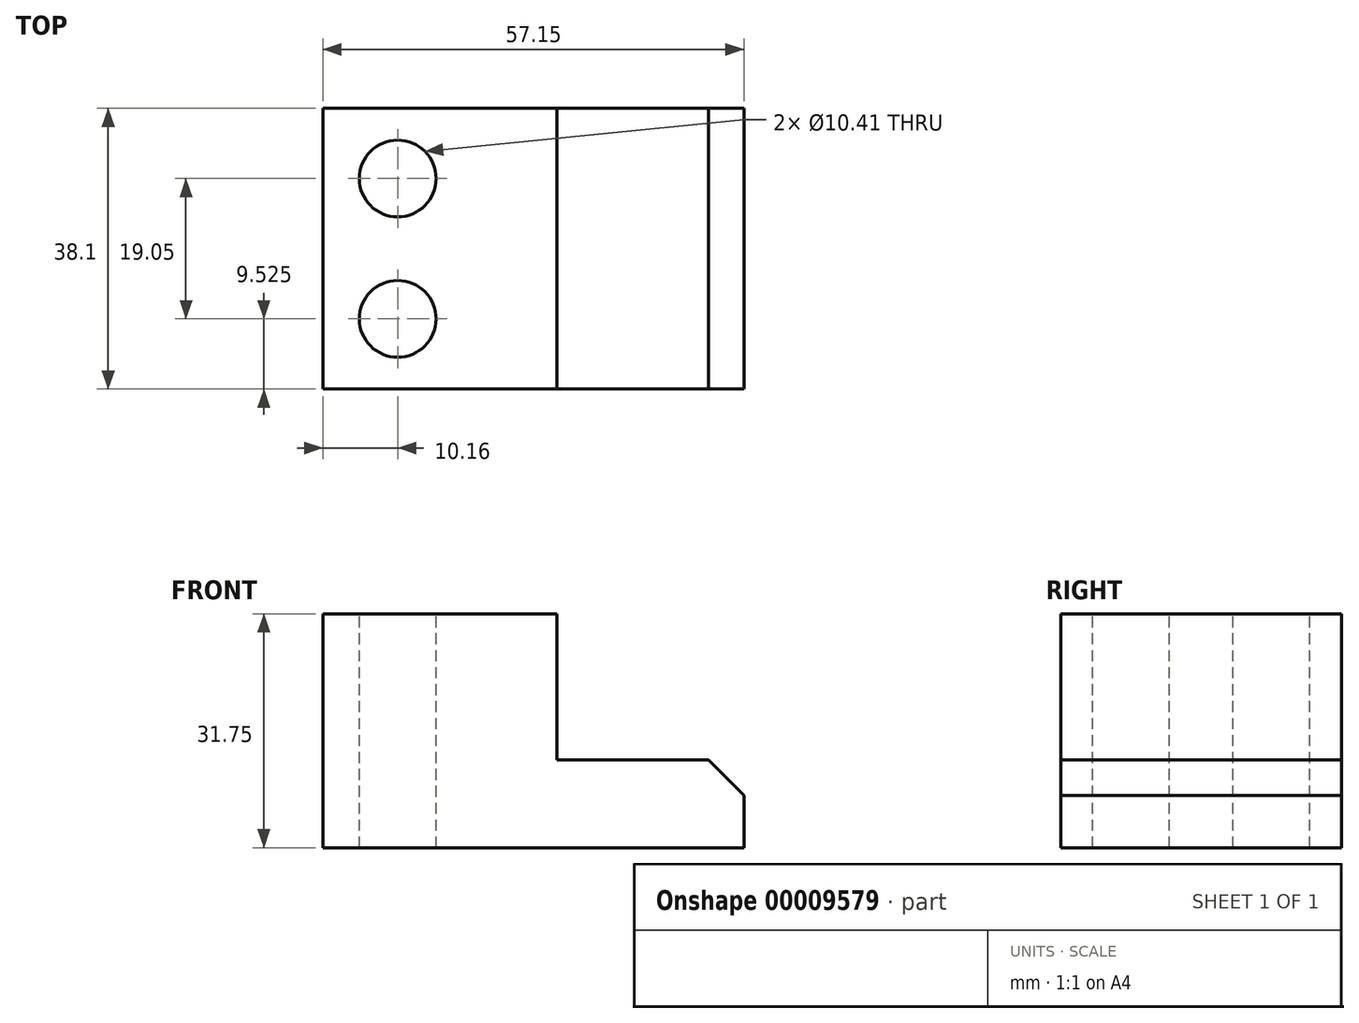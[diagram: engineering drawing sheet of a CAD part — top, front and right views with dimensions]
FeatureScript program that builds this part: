
annotation { "Feature Type Name" : "Feature", "Feature Type Description" : "" }
export const myFeature = defineFeature(function(context is Context, id is Id, definition is map)
    precondition{}
    {
        {
            var Q0;
            Q0=qCreatedBy(makeId("Front.planeOp"),FACE);
            var sketch = newSketch(context, id + "F0", { "sketchPlane" : qUnion([Q0])});
            skLineSegment(sketch, "E0.bottom", {"start": v(0, 0) * mm, "end": v(31.75, 0) * mm});
            skLineSegment(sketch, "E0.top", {"start": v(0, -31.75) * mm, "end": v(57.15, -31.75) * mm});
            skLineSegment(sketch, "E0.left", {"start": v(0, 0) * mm, "end": v(0, -31.75) * mm});
            skLineSegment(sketch, "E1.top", {"start": v(31.75, -19.81) * mm, "end": v(57.15, -19.81) * mm});
            skLineSegment(sketch, "E1.left", {"start": v(31.75, 0) * mm, "end": v(31.75, -19.81) * mm});
            skLineSegment(sketch, "E2", {"start": v(57.15, -19.81) * mm, "end": v(57.15, -31.75) * mm});
            skSolve(sketch);
        }
        {
            var Q0;
            Q0 = qSketchRegion(id + "F0", true);
            extrude(context, id + "F1", {"entities" : qUnion([Q0]), "depth" : 38.1 * mm});
        }
        {
            var Q0;
            Q0=makeQuery(id+"F1.opExtrude","SWEPT_EDGE",EDGE,{"disambiguationData":[OSD([sQuery(id+"F0.wireOp",EDGE,"E1.top"),sQuery(id+"F0.wireOp",EDGE,"E2")])]});
            chamfer(context, id + "F2", {"entities" : qUnion([Q0]), "width" : 4.83 * mm, "tangentPropagation" : true});
        }
        {
            var Q0;
            Q0=makeQuery(id+"F1.opExtrude","SWEPT_FACE",FACE,{"disambiguationData":[OSD([sQuery(id+"F0.wireOp",EDGE,"E0.bottom")])]});
            var sketch = newSketch(context, id + "F3", { "sketchPlane" : qUnion([Q0])});
            skCircle(sketch, "E3", {"center": v(10.16, -9.53) * mm, "radius": 5.2 * mm});
            skCircle(sketch, "E4", {"center": v(10.16, -28.58) * mm, "radius": 5.2 * mm});
            skSolve(sketch);
        }
        {
            var Q0;
            Q0 = qSketchRegion(id + "F3", true);
            extrude(context, id + "F4", {"entities" : qUnion([Q0]), "operationType" : NewBodyOperationType.REMOVE, "endBound" : BoundingType.THROUGH_ALL, "oppositeDirection" : true, "depth" : 25.4 * mm});
        }
    });
